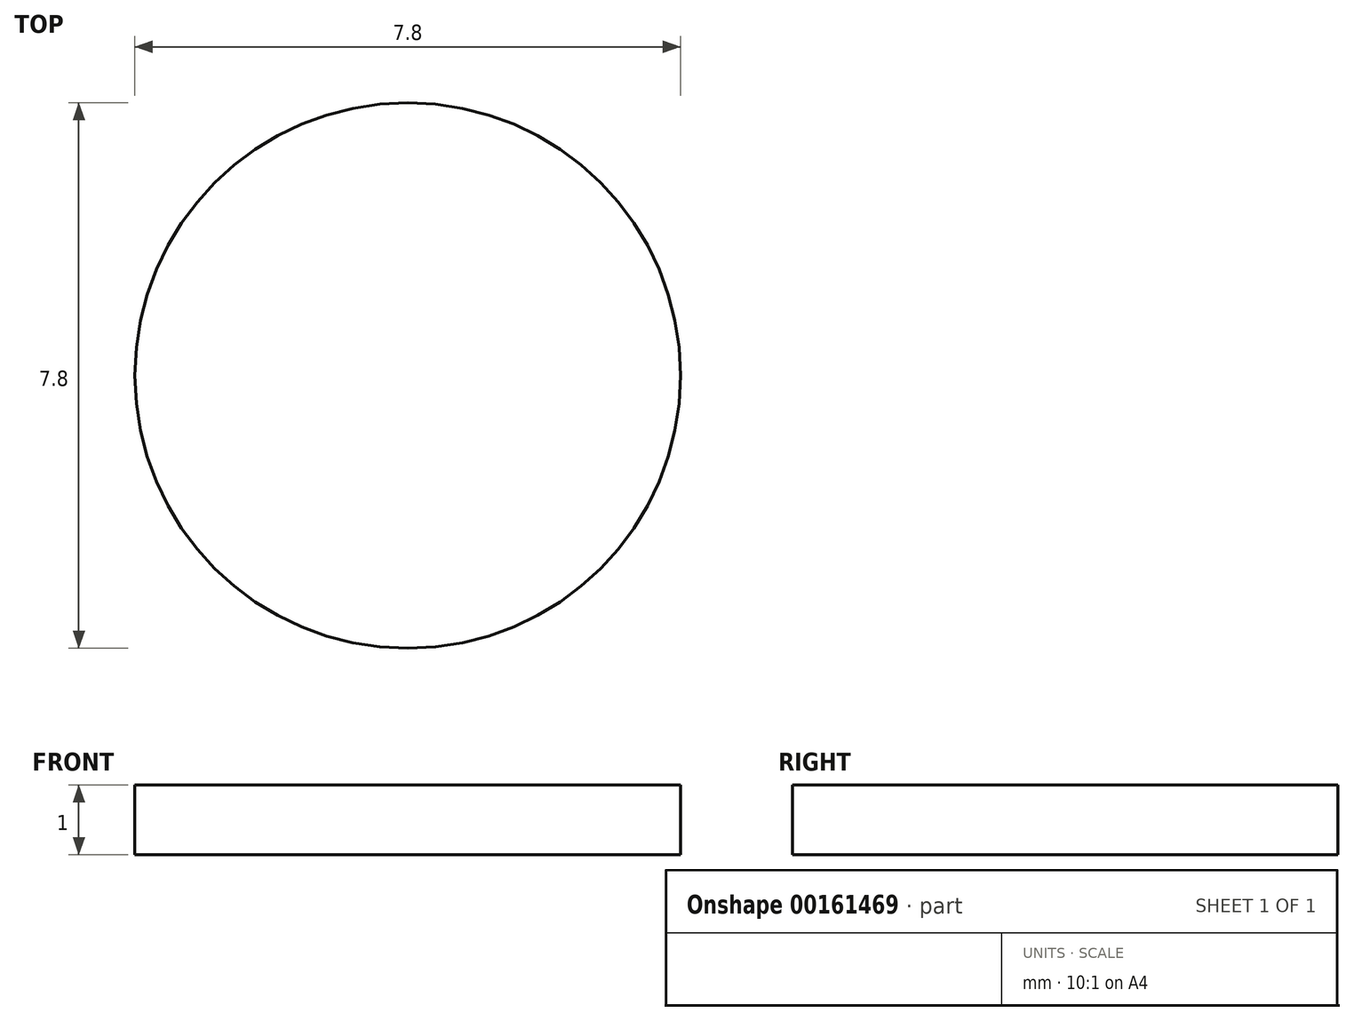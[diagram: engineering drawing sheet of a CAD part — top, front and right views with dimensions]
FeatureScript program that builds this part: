
annotation { "Feature Type Name" : "Feature", "Feature Type Description" : "" }
export const myFeature = defineFeature(function(context is Context, id is Id, definition is map)
    precondition{}
    {
        {
            assignVariable(context, id + "F0", {"name" : "Main_Thickness", "anyValue" : 1});
        }
        {
            var Q0;
            Q0=qCreatedBy(makeId("Top.planeOp"),FACE);
            var sketch = newSketch(context, id + "F1", { "sketchPlane" : qUnion([Q0])});
            skCircle(sketch, "E0", {"center": v(0, 0) * mm, "radius": 3.9 * mm});
            skSolve(sketch);
        }
        {
            var Q0;
            Q0=makeQuery(id+"F1.imprint","IMPRINT",FACE,{"disambiguationData":[TD([[makeQuery(id+"F1.imprint","IMPRINT",EDGE,{"derivedFrom":sQuery(id+"F1.wireOp",EDGE,"E0")}),1.0]])]});
            var Q1;
            Q1=sQuery(id+"F1.wireOp",EDGE,"E0");
            extrude(context, id + "F2", {"entities" : qUnion([Q0]), "surfaceEntities" : qUnion([Q1]), "depth" : (getVariable(context, 'Main_Thickness')) * mm});
        }
    });
